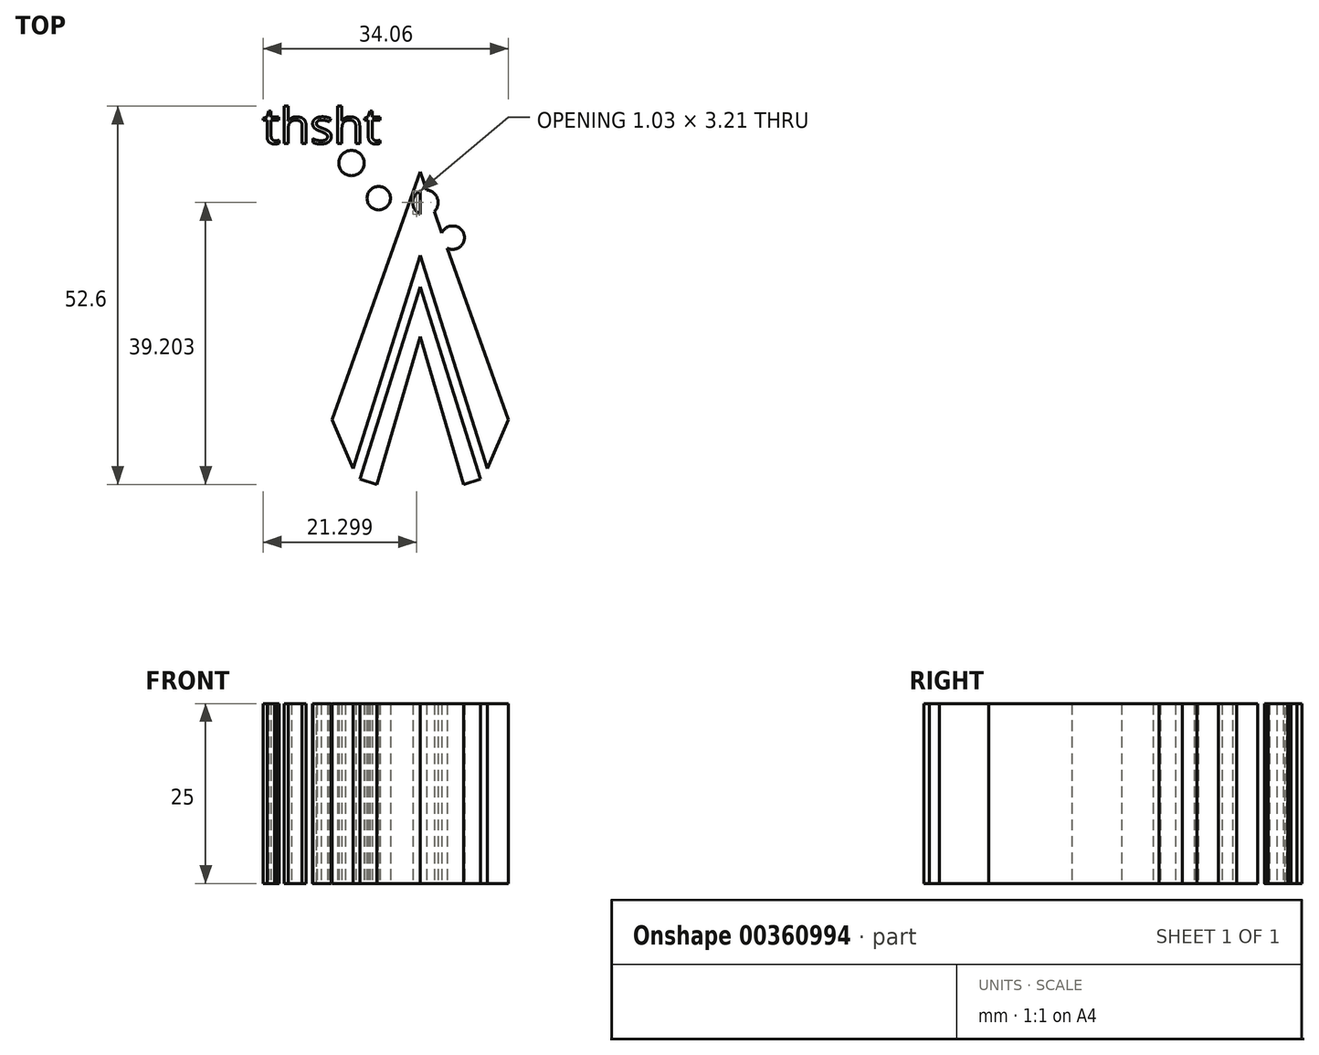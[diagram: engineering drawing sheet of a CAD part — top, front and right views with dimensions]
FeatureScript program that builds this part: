
annotation { "Feature Type Name" : "Feature", "Feature Type Description" : "" }
export const myFeature = defineFeature(function(context is Context, id is Id, definition is map)
    precondition{}
    {
        {
            var Q0;
            Q0=qCreatedBy(makeId("Top.planeOp"),FACE);
            var sketch = newSketch(context, id + "F0", { "sketchPlane" : qUnion([Q0])});
            skLineSegment(sketch, "E0", {"start": v(-11.64, 4.76) * mm, "end": v(-11.64, -38.64) * mm});
            skLineSegment(sketch, "E1", {"start": v(-11.64, 4.76) * mm, "end": v(-23.89, -29.71) * mm});
            skLineSegment(sketch, "E2", {"start": v(-23.89, -29.71) * mm, "end": v(-20.96, -36.53) * mm});
            skLineSegment(sketch, "E3", {"start": v(-20.96, -36.53) * mm, "end": v(-11.64, -6.84) * mm});
            skLineSegment(sketch, "E4", {"start": v(-11.64, -11.24) * mm, "end": v(-20.03, -37.97) * mm});
            skLineSegment(sketch, "E5", {"start": v(-20.03, -37.97) * mm, "end": v(-17.67, -38.7) * mm});
            skLineSegment(sketch, "E6", {"start": v(-17.67, -38.7) * mm, "end": v(-11.64, -18.16) * mm});
            skLineSegment(sketch, "E7", {"start": v(-11.64, -18.16) * mm, "end": v(-11.64, -11.24) * mm});
            skLineSegment(sketch, "E8.MirrorCS", {"start": v(-11.64, 4.76) * mm, "end": v(0.6, -29.71) * mm});
            skLineSegment(sketch, "E9.MirrorCS", {"start": v(-2.33, -36.53) * mm, "end": v(-11.64, -6.84) * mm});
            skLineSegment(sketch, "E10.MirrorCS", {"start": v(0.6, -29.71) * mm, "end": v(-2.33, -36.53) * mm});
            skLineSegment(sketch, "E11.MirrorCS", {"start": v(-11.64, -11.24) * mm, "end": v(-3.26, -37.97) * mm});
            skLineSegment(sketch, "E12.MirrorCS", {"start": v(-5.62, -38.7) * mm, "end": v(-11.64, -18.16) * mm});
            skLineSegment(sketch, "E13.MirrorCS", {"start": v(-3.26, -37.97) * mm, "end": v(-5.62, -38.7) * mm});
            skCircle(sketch, "E14", {"center": v(-7.12, -4.4) * mm, "radius": 1.63 * mm});
            skCircle(sketch, "E15", {"center": v(-10.92, 0.5) * mm, "radius": 1.76 * mm});
            skCircle(sketch, "E16", {"center": v(-17.4, 1.1) * mm, "radius": 1.63 * mm});
            skCircle(sketch, "E17", {"center": v(-21.2, 5.98) * mm, "radius": 1.76 * mm});
            skText(sketch, "E18", { "text": "thsht\n\n", "fontName": "OpenSans-Regular.ttf"});
            const initialGuessF0  = {"E18": [-0.03356, 0.0087, 1, 0, 0.00492]};
            skSetInitialGuess(sketch, initialGuessF0);
            skSolve(sketch);
        }
        {
            var Q0;
            Q0 = qSketchRegion(id + "F0", true);
            extrude(context, id + "F1", {"entities" : qUnion([Q0]), "depth" : 25 * mm});
        }
    });
